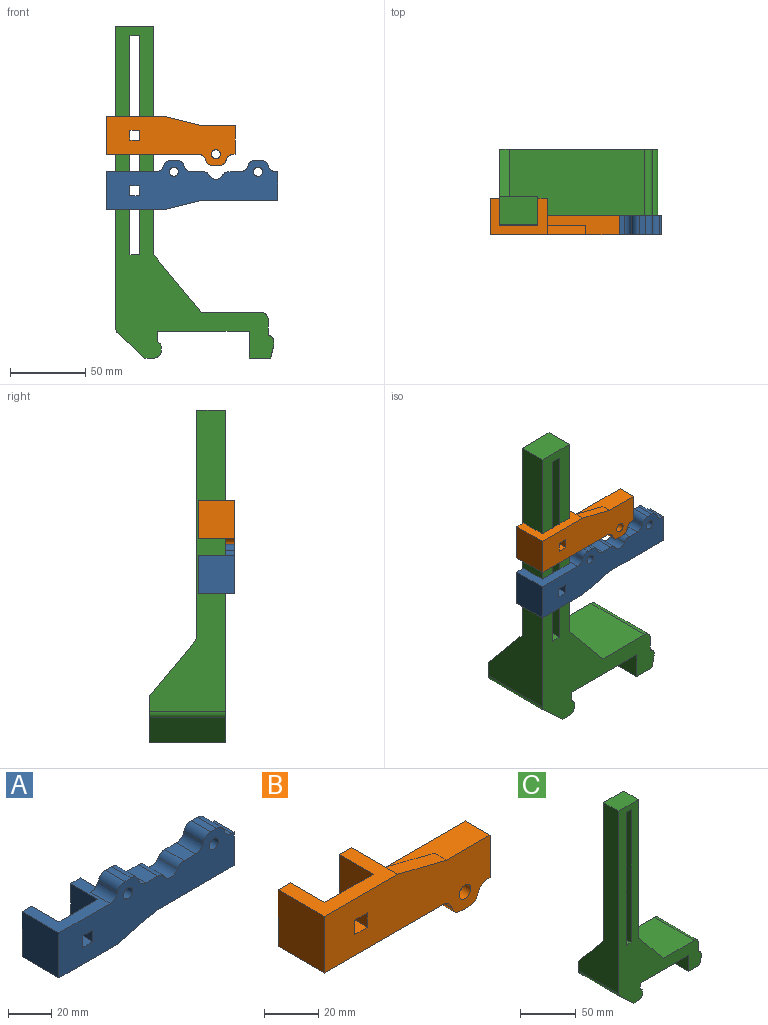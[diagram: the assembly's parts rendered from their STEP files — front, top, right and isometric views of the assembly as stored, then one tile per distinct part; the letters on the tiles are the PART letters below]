
ASSEMBLY  parts=3 mates=2
PART A: 51 faces, bbox 114.3x24.1x33 mm
  f0: plane 80.91x26.67mm, normal (0,1,0), area 1440.6mm2, adj f3,f4,f5,f6,f7,f15,f21,f24
  f1: cylinder r=3.02mm len=8.7mm, axis (0,-1,0), area 165.4mm2, adj f8,f40
  f2: cylinder r=3.02mm len=8.7mm, axis (0,-1,0), area 165.4mm2, adj f8,f33
  f3: plane 12.7x7.63mm, normal (0,0,1), area 96.9mm2, adj f0,f8,f31,f49
  f4: plane 12.7x7.63mm, normal (0,0,1), area 96.9mm2, adj f0,f8,f32,f48
  f5: plane 38.1x24.13mm, normal (0,0,1), area 407.9mm2, adj f0,f7,f8,f9,f10,f11,f12,f13
  f6: plane 76.2x12.7mm, normal (0,0,-1), area 806.4mm2, adj f0,f7,f8,f21,f22,f23
  f7: plane 25.4x17.78mm, normal (1,0,0), area 330.6mm2, adj f0,f5,f6,f10,f16,f23
  f8: plane 114.3x33.02mm, normal (0,-1,0), area 2565.9mm2, adj f1,f2,f3,f4,f5,f6,f14,f15
  f9: plane 25.4x25.4mm, normal (0,1,0), area 602.9mm2, adj f5,f11,f12,f16,f17,f18,f19,f20
  f10: plane 25.4x6.35mm, normal (0,1,0), area 161.3mm2, adj f5,f7,f11,f16
  f11: plane 25.4x17.78mm, normal (-1,0,0), area 451.6mm2, adj f5,f9,f10,f16
  f12: plane 25.4x17.78mm, normal (1,0,0), area 451.6mm2, adj f5,f9,f13,f16
  f13: plane 25.4x6.35mm, normal (0,1,0), area 161.3mm2, adj f5,f12,f14,f16
  f14: plane 25.4x24.13mm, normal (-1,0,0), area 612.9mm2, adj f5,f8,f13,f16
  f15: plane 12.7x1.49mm, normal (0,0,1), area 18.9mm2, adj f0,f8,f21,f47
  f16: plane 38.1x24.13mm, normal (0,0,-1), area 467.7mm2, adj f7,f8,f9,f10,f11,f12,f13,f14
  f17: plane 6.5x6.35mm, normal (0,0,1), area 41.3mm2, adj f8,f9,f18,f20
  f18: plane 6.5x6.35mm, normal (-1,0,0), area 41.3mm2, adj f8,f9,f17,f19
  f19: plane 6.5x6.35mm, normal (0,0,-1), area 41.3mm2, adj f8,f9,f18,f20
  f20: plane 6.5x6.35mm, normal (1,0,0), area 41.3mm2, adj f8,f9,f17,f19
  f21: plane 19.05x12.7mm, normal (1,0,0), area 241.9mm2, adj f0,f6,f8,f15
  f22: plane 25.4x6.35mm, normal (0.24,0,-0.97), area 166.3mm2, adj f6,f8,f16,f23
  f23: plane 25.4x6.35mm, normal (0,1,0), area 80.6mm2, adj f6,f7,f22
  f24: plane 12.7x4mm, normal (0,0,1), area 50.8mm2, adj f0,f8,f28,f29
  f25: plane 12.7x4mm, normal (0,0,1), area 50.8mm2, adj f0,f8,f26,f27
  f26: cylinder r=5mm len=12.7mm, axis (0,-1,0), area 84.5mm2, adj f0,f8,f25,f47
  f27: cylinder r=5mm len=12.7mm, axis (0,1,0), area 84.5mm2, adj f0,f8,f25,f48
  f28: cylinder r=5mm len=12.7mm, axis (0,-1,0), area 84.5mm2, adj f0,f8,f24,f49
  f29: cylinder r=5mm len=12.7mm, axis (0,1,0), area 84.5mm2, adj f0,f8,f24,f50
  f30: cylinder r=5mm len=12.7mm, axis (0,-1,0), area 133mm2, adj f0,f8,f31,f32
  f31: cylinder r=5mm len=12.7mm, axis (0,-1,0), area 66.5mm2, adj f0,f3,f8,f30
  f32: cylinder r=5mm len=12.7mm, axis (0,-1,0), area 66.5mm2, adj f0,f4,f8,f30
  f33: plane 11.66x10.1mm, normal (0,1,0), area 59.6mm2, adj f2,f34,f35,f36,f37,f38,f39
  f34: plane 5.05x4mm, normal (-0.87,0,0.5), area 23.3mm2, adj f0,f33,f35,f39
  f35: plane 5.83x4mm, normal (0,0,1), area 23.3mm2, adj f0,f33,f34,f36
  f36: plane 5.05x4mm, normal (0.87,0,0.5), area 23.3mm2, adj f0,f33,f35,f37
  f37: plane 5.05x4mm, normal (0.87,0,-0.5), area 23.3mm2, adj f0,f33,f36,f38
  f38: plane 5.83x4mm, normal (0,0,-1), area 23.3mm2, adj f0,f33,f37,f39
  f39: plane 5.05x4mm, normal (-0.87,0,-0.5), area 23.3mm2, adj f0,f33,f34,f38
  f40: plane 11.66x10.1mm, normal (0,1,0), area 59.6mm2, adj f1,f41,f42,f43,f44,f45,f46
  f41: plane 5.05x4mm, normal (0.87,0,-0.5), area 23.3mm2, adj f0,f40,f42,f46
  f42: plane 5.83x4mm, normal (0,0,-1), area 23.3mm2, adj f0,f40,f41,f43
  f43: plane 5.05x4mm, normal (-0.87,0,-0.5), area 23.3mm2, adj f0,f40,f42,f44
  f44: plane 5.05x4mm, normal (-0.87,0,0.5), area 23.3mm2, adj f0,f40,f43,f45
  f45: plane 5.83x4mm, normal (0,0,1), area 23.3mm2, adj f0,f40,f44,f46
  f46: plane 5.05x4mm, normal (0.87,0,0.5), area 23.3mm2, adj f0,f40,f41,f45
  f47: cylinder r=5mm len=12.7mm, axis (0,-1,0), area 84.5mm2, adj f0,f8,f15,f26
  f48: cylinder r=5mm len=12.7mm, axis (0,1,0), area 84.5mm2, adj f0,f4,f8,f27
  f49: cylinder r=5mm len=12.7mm, axis (0,-1,0), area 84.5mm2, adj f0,f3,f8,f28
  f50: cylinder r=5mm len=12.7mm, axis (0,1,0), area 84.5mm2, adj f0,f5,f8,f29
PART B: 33 faces, bbox 86.1x24.1x33 mm
  f0: plane 25.4x24.13mm, normal (-1,0,0), area 612.9mm2, adj f1,f2,f5,f32
  f1: plane 38.1x24.13mm, normal (0,0,1), area 467.7mm2, adj f0,f5,f6,f7,f8,f9,f16,f31
  f2: plane 61.39x24.13mm, normal (0,0,-1), area 763.5mm2, adj f0,f3,f5,f6,f7,f8,f9,f30
  f3: plane 48x26.67mm, normal (0,1,0), area 928.8mm2, adj f2,f4,f9,f14,f15,f18,f19,f20
  f4: plane 12.7x1.29mm, normal (0,0,-1), area 16.3mm2, adj f3,f5,f14,f29
  f5: plane 86.1x33.02mm, normal (0,-1,0), area 1996.3mm2, adj f0,f1,f2,f4,f10,f11,f12,f13
  f6: plane 25.4x25.4mm, normal (0,1,0), area 602.9mm2, adj f1,f2,f7,f8,f10,f11,f12,f13
  f7: plane 25.4x17.78mm, normal (-1,0,0), area 451.6mm2, adj f1,f2,f6,f31
  f8: plane 25.4x17.78mm, normal (1,0,0), area 451.6mm2, adj f1,f2,f6,f32
  f9: plane 25.4x17.78mm, normal (1,0,0), area 330.6mm2, adj f1,f2,f3,f15,f17,f31
  f10: plane 6.5x6.35mm, normal (0,0,1), area 41.3mm2, adj f5,f6,f11,f13
  f11: plane 6.5x6.35mm, normal (-1,0,0), area 41.3mm2, adj f5,f6,f10,f12
  f12: plane 6.5x6.35mm, normal (0,0,-1), area 41.3mm2, adj f5,f6,f11,f13
  f13: plane 6.5x6.35mm, normal (1,0,0), area 41.3mm2, adj f5,f6,f10,f12
  f14: plane 19.05x12.7mm, normal (1,0,0), area 241.9mm2, adj f3,f4,f5,f15
  f15: plane 48x12.7mm, normal (0,0,1), area 448.3mm2, adj f3,f5,f9,f14,f16,f17
  f16: plane 25.4x6.35mm, normal (0.24,0,0.97), area 166.3mm2, adj f1,f5,f15,f17
  f17: plane 25.4x6.35mm, normal (0,1,0), area 80.6mm2, adj f9,f15,f16
  f18: plane 12.7x4mm, normal (0,0,-1), area 50.8mm2, adj f3,f5,f19,f20
  f19: cylinder r=5mm len=12.7mm, axis (0,1,0), area 84.5mm2, adj f3,f5,f18,f29
  f20: cylinder r=5mm len=12.7mm, axis (0,-1,0), area 84.5mm2, adj f3,f5,f18,f30
  f21: cylinder r=3.02mm len=8.7mm, axis (0,1,0), area 165.4mm2, adj f5,f28
  f22: plane 5.1x4mm, normal (0.87,0,0.5), area 23.6mm2, adj f3,f23,f27,f28
  f23: plane 5.1x4mm, normal (0.87,0,-0.5), area 23.6mm2, adj f3,f22,f24,f28
  f24: plane 5.89x4mm, normal (0,0,-1), area 23.6mm2, adj f3,f23,f25,f28
  f25: plane 5.1x4mm, normal (-0.87,0,-0.5), area 23.6mm2, adj f3,f24,f26,f28
  f26: plane 5.1x4mm, normal (-0.87,0,0.5), area 23.6mm2, adj f3,f25,f27,f28
  f27: plane 5.89x4mm, normal (0,0,1), area 23.6mm2, adj f3,f22,f26,f28
  f28: plane 11.78x10.2mm, normal (0,1,0), area 61.4mm2, adj f21,f22,f23,f24,f25,f26,f27
  f29: cylinder r=5mm len=12.7mm, axis (0,1,0), area 84.5mm2, adj f3,f4,f5,f19
  f30: cylinder r=5mm len=12.7mm, axis (0,-1,0), area 84.5mm2, adj f2,f3,f5,f20
  f31: plane 25.4x6.35mm, normal (0,1,0), area 161.3mm2, adj f1,f2,f7,f9
  f32: plane 25.4x6.35mm, normal (0,1,0), area 161.3mm2, adj f0,f1,f2,f8
PART C: 40 faces, bbox 105.4x50.8x221 mm
  f0: plane 50.8x1.12mm, normal (1,0,0), area 56.7mm2, adj f2,f3,f27,f36
  f1: plane 50.8x17.76mm, normal (-1,0,0), area 811.5mm2, adj f2,f3,f10,f28,f29,f30,f31,f32
  f2: plane 220.96x105.36mm, normal (0,-1,0), area 6409.1mm2, adj f0,f1,f4,f5,f7,f8,f9,f10
  f3: plane 105.36x30.46mm, normal (0,1,0), area 1892.9mm2, adj f0,f1,f4,f5,f7,f9,f10,f11
  f4: plane 50.8x8.69mm, normal (0.97,0,-0.24), area 423.9mm2, adj f2,f3,f34,f36,f38
  f5: plane 50.8x10.16mm, normal (1,0,0), area 516.1mm2, adj f2,f3,f16,f27
  f6: plane 190.5x25.4mm, normal (0,1,0), area 3669.3mm2, adj f7,f8,f9,f18,f19,f20,f23,f24
  f7: plane 90.17x50.8mm, normal (0,0,1), area 4016.1mm2, adj f2,f3,f6,f8,f16,f20,f21,f22
  f8: plane 190.5x19.05mm, normal (1,0,0), area 3387.1mm2, adj f2,f6,f7,f18,f21,f22
  f9: plane 200.96x50.8mm, normal (-1,0,0), area 4765.2mm2, adj f2,f3,f6,f15,f18,f19
  f10: plane 61.21x50.8mm, normal (0,0,-1), area 3109.7mm2, adj f1,f2,f3,f14
  f11: plane 50.8x2.37mm, normal (0.97,0,0.25), area 124.3mm2, adj f2,f3,f12,f39
  f12: plane 50.8x1.97mm, normal (1,0,0), area 99.8mm2, adj f2,f3,f11,f17
  f13: plane 50.8x17.81mm, normal (-0.67,0,-0.74), area 1224.7mm2, adj f2,f3,f15,f37
  f14: plane 50.8x5.48mm, normal (1,0,0), area 278.5mm2, adj f2,f3,f10,f39
  f15: cylinder r=5.08mm len=50.8mm, axis (0,-1,0), area 214.4mm2, adj f2,f3,f9,f13
  f16: cylinder r=5.08mm len=50.8mm, axis (0,1,0), area 405.4mm2, adj f2,f3,f5,f7
  f17: cylinder r=5.08mm len=50.8mm, axis (0,1,0), area 384.7mm2, adj f2,f3,f12,f37
  f18: plane 25.4x19.05mm, normal (0,0,1), area 483.9mm2, adj f2,f6,f8,f9
  f19: plane 38.1x31.75mm, normal (0,0.77,0.64), area 314.9mm2, adj f3,f6,f9,f20
  f20: plane 38.1x31.75mm, normal (1,0,0), area 604.8mm2, adj f6,f7,f19
  f21: plane 38.1x31.75mm, normal (0.77,0,0.64), area 314.9mm2, adj f2,f7,f8,f22
  f22: plane 38.1x31.75mm, normal (0,1,0), area 604.8mm2, adj f7,f8,f21
  f23: plane 19.05x6.35mm, normal (0,0,1), area 121mm2, adj f2,f6,f24,f26
  f24: plane 146.05x19.05mm, normal (1,0,0), area 2782.3mm2, adj f2,f6,f23,f25
  f25: plane 19.05x6.35mm, normal (0,0,-1), area 121mm2, adj f2,f6,f24,f26
  f26: plane 146.05x19.05mm, normal (-1,0,0), area 2782.3mm2, adj f2,f6,f23,f25
  f27: cylinder r=5mm len=50.8mm, axis (0,-1,0), area 335.2mm2, adj f0,f2,f3,f5
  f28: plane 7.77x6.8mm, normal (-0.12,0.87,-0.49), area 43mm2, adj f1,f30,f32,f35
  f29: plane 7.77x6.8mm, normal (-0.12,-0.87,-0.49), area 43mm2, adj f1,f30,f33,f35
  f30: plane 7.77x5.83mm, normal (-0.24,0,-0.97), area 46.6mm2, adj f1,f28,f29,f35
  f31: plane 5.83x5.38mm, normal (0.24,0,0.97), area 32.3mm2, adj f1,f32,f33,f35
  f32: plane 6.57x6.51mm, normal (0.12,0.87,0.49), area 35.9mm2, adj f1,f28,f31,f35
  f33: plane 6.57x6.51mm, normal (0.12,-0.87,0.49), area 35.9mm2, adj f1,f29,f31,f35
  f34: cylinder r=3.12mm len=10.22mm, axis (0.97,0,-0.24), area 176.7mm2, adj f4,f35
  f35: plane 11.66x9.81mm, normal (-0.97,0,0.24), area 57.7mm2, adj f28,f29,f30,f31,f32,f33,f34
  f36: cylinder r=3mm len=50.8mm, axis (0,1,0), area 29.3mm2, adj f0,f2,f3,f4
  f37: plane 50.8x6.34mm, normal (0,0,-1), area 322.3mm2, adj f2,f3,f13,f17
  f38: plane 50.8x14.26mm, normal (0,0,-1), area 724.3mm2, adj f1,f2,f3,f4
  f39: cylinder r=3mm len=50.8mm, axis (0,1,0), area 197.1mm2, adj f2,f3,f11,f14
PLACE A t=(-38.35,-15.62,96.04)mm
PLACE B t=(-38.1,-15.62,133.04)mm
PLACE C at identity
MATE slider B.f1 <-> C.f18  axis (0,0,1) through (-25.4,-25.4,145.74)mm
MATE slider A.f5 <-> C.f18  axis (0,0,1) through (-50.8,-25.4,108.74)mm
